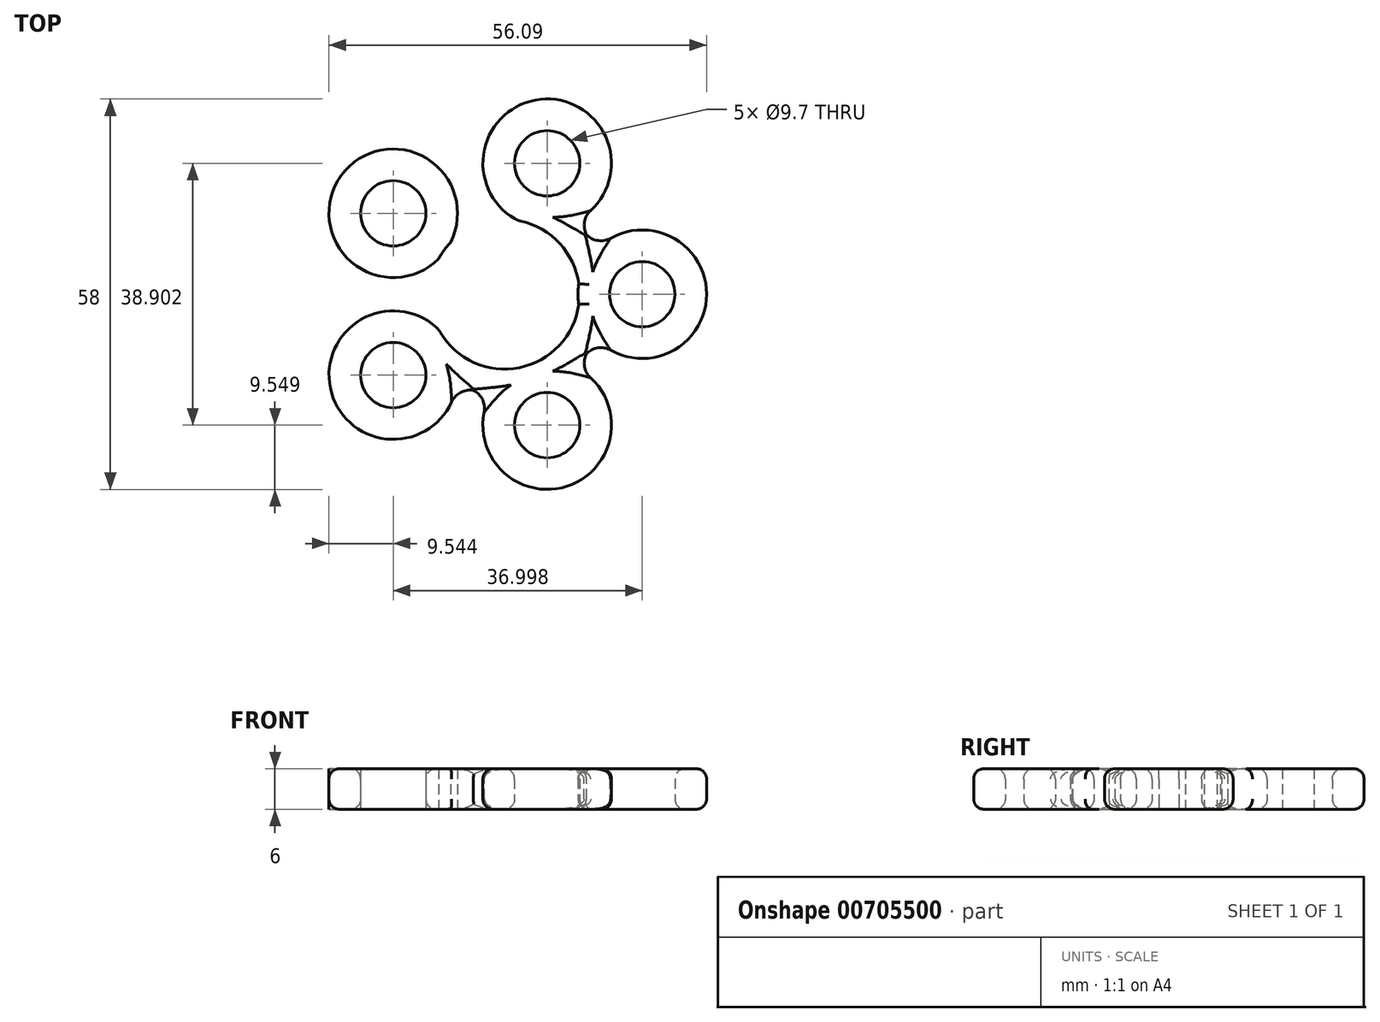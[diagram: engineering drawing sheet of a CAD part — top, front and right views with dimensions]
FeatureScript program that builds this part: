
annotation { "Feature Type Name" : "Feature", "Feature Type Description" : "" }
export const myFeature = defineFeature(function(context is Context, id is Id, definition is map)
    precondition{}
    {
        {
            var Q0;
            Q0=qCreatedBy(makeId("Top.planeOp"),FACE);
            var sketch = newSketch(context, id + "F0", { "sketchPlane" : qUnion([Q0])});
            skCircle(sketch, "E0", {"center": v(0, 0) * mm, "radius": 11.13 * mm});
            skCircle(sketch, "E1", {"center": v(0, 0) * mm, "radius": 15 * mm});
            skLineSegment(sketch, "E2", {"start": v(0, 0) * mm, "end": v(30, 0) * mm, "construction": true});
            skCircle(sketch, "E3", {"center": v(20.45, 0) * mm, "radius": 4.85 * mm});
            skCircle(sketch, "E4", {"center": v(20.45, 0) * mm, "radius": 9.55 * mm});
            skLineSegment(sketch, "E5.1.1", {"start": v(0, 0) * mm, "end": v(9.27, 28.53) * mm, "construction": true});
            skCircle(sketch, "E5.1.2", {"center": v(6.32, 19.45) * mm, "radius": 4.85 * mm});
            skCircle(sketch, "E5.1.3", {"center": v(6.32, 19.45) * mm, "radius": 9.55 * mm});
            skLineSegment(sketch, "E5.2.1", {"start": v(0, 0) * mm, "end": v(-24.27, 17.63) * mm, "construction": true});
            skCircle(sketch, "E5.2.2", {"center": v(-16.55, 12.02) * mm, "radius": 4.85 * mm});
            skCircle(sketch, "E5.2.3", {"center": v(-16.55, 12.02) * mm, "radius": 9.55 * mm});
            skLineSegment(sketch, "E6.2.3.0", {"start": v(0, 0) * mm, "end": v(-24.27, -17.63) * mm, "construction": true});
            skCircle(sketch, "E6.5.3.0", {"center": v(-16.55, -12.02) * mm, "radius": 4.85 * mm});
            skCircle(sketch, "E6.7.3.0", {"center": v(-16.55, -12.02) * mm, "radius": 9.55 * mm});
            skLineSegment(sketch, "E6.2.4.0", {"start": v(0, 0) * mm, "end": v(9.27, -28.53) * mm, "construction": true});
            skCircle(sketch, "E6.5.4.0", {"center": v(6.32, -19.45) * mm, "radius": 4.85 * mm});
            skCircle(sketch, "E6.7.4.0", {"center": v(6.32, -19.45) * mm, "radius": 9.55 * mm});
            skSolve(sketch);
        }
        {
            var Q0;
            {var subQ0=sQuery(id+"F0.wireOp",EDGE,"E1");var subQ1=sQuery(id+"F0.wireOp",EDGE,"E5.2.3");var subQ2=makeQuery(id+"F0.imprint","INTERSECT",VERTEX,{"disambiguationData":[OD(0.0)],"derivedFrom":[subQ1,subQ0]});Q0=makeQuery(id+"F0.imprint","IMPRINT",FACE,{"disambiguationData":[TD([[makeQuery(id+"F0.imprint","IMPRINT",EDGE,{"disambiguationData":[TD([[subQ2,-1.0]])],"derivedFrom":subQ1}),1.0]])]});}
            var Q1;
            {var subQ0=sQuery(id+"F0.wireOp",EDGE,"E1");var subQ1=sQuery(id+"F0.wireOp",EDGE,"E6.7.3.0");var subQ2=makeQuery(id+"F0.imprint","INTERSECT",VERTEX,{"disambiguationData":[OD(0.0)],"derivedFrom":[subQ1,subQ0]});Q1=makeQuery(id+"F0.imprint","IMPRINT",FACE,{"disambiguationData":[TD([[makeQuery(id+"F0.imprint","IMPRINT",EDGE,{"disambiguationData":[TD([[subQ2,-1.0]])],"derivedFrom":subQ1}),1.0]])]});}
            var Q2;
            {var subQ0=sQuery(id+"F0.wireOp",EDGE,"E1");var subQ1=sQuery(id+"F0.wireOp",EDGE,"E5.1.3");var subQ2=makeQuery(id+"F0.imprint","INTERSECT",VERTEX,{"disambiguationData":[OD(0.0)],"derivedFrom":[subQ1,subQ0]});Q2=makeQuery(id+"F0.imprint","IMPRINT",FACE,{"disambiguationData":[TD([[makeQuery(id+"F0.imprint","IMPRINT",EDGE,{"disambiguationData":[TD([[subQ2,-1.0]])],"derivedFrom":subQ1}),1.0]])]});}
            var Q3;
            {var subQ0=sQuery(id+"F0.wireOp",EDGE,"E1");var subQ1=sQuery(id+"F0.wireOp",EDGE,"E6.7.3.0");var subQ2=makeQuery(id+"F0.imprint","INTERSECT",VERTEX,{"disambiguationData":[OD(0.0)],"derivedFrom":[subQ1,subQ0]});Q3=makeQuery(id+"F0.imprint","IMPRINT",FACE,{"disambiguationData":[TD([[makeQuery(id+"F0.imprint","IMPRINT",EDGE,{"disambiguationData":[TD([[subQ2,-1.0]])],"derivedFrom":subQ1}),-1.0]])]});}
            var Q4;
            {var subQ0=sQuery(id+"F0.wireOp",EDGE,"E1");var subQ1=sQuery(id+"F0.wireOp",EDGE,"E4");var subQ2=makeQuery(id+"F0.imprint","INTERSECT",VERTEX,{"disambiguationData":[OD(0.0)],"derivedFrom":[subQ1,subQ0]});Q4=makeQuery(id+"F0.imprint","IMPRINT",FACE,{"disambiguationData":[TD([[makeQuery(id+"F0.imprint","IMPRINT",EDGE,{"disambiguationData":[TD([[subQ2,-1.0]])],"derivedFrom":subQ1}),1.0]])]});}
            var Q5;
            {var subQ0=sQuery(id+"F0.wireOp",EDGE,"E6.7.4.0");var subQ1=sQuery(id+"F0.wireOp",EDGE,"E1");var subQ2=makeQuery(id+"F0.imprint","INTERSECT",VERTEX,{"disambiguationData":[OD(0.0)],"derivedFrom":[subQ1,subQ0]});Q5=makeQuery(id+"F0.imprint","IMPRINT",FACE,{"disambiguationData":[TD([[makeQuery(id+"F0.imprint","IMPRINT",EDGE,{"disambiguationData":[TD([[subQ2,1.0]])],"derivedFrom":subQ1}),1.0]])]});}
            var Q6;
            Q6=makeQuery(id+"F0.imprint","IMPRINT",FACE,{"disambiguationData":[TD([[makeQuery(id+"F0.imprint","IMPRINT",EDGE,{"derivedFrom":sQuery(id+"F0.wireOp",EDGE,"E5.2.2")}),-1.0]])]});
            var Q7;
            {var subQ0=sQuery(id+"F0.wireOp",EDGE,"E1");var subQ1=sQuery(id+"F0.wireOp",EDGE,"E5.2.3");var subQ2=makeQuery(id+"F0.imprint","INTERSECT",VERTEX,{"disambiguationData":[OD(0.0)],"derivedFrom":[subQ1,subQ0]});Q7=makeQuery(id+"F0.imprint","IMPRINT",FACE,{"disambiguationData":[TD([[makeQuery(id+"F0.imprint","IMPRINT",EDGE,{"disambiguationData":[TD([[subQ2,-1.0]])],"derivedFrom":subQ1}),-1.0]])]});}
            var Q8;
            {var subQ0=sQuery(id+"F0.wireOp",EDGE,"E1");var subQ1=sQuery(id+"F0.wireOp",EDGE,"E4");var subQ2=makeQuery(id+"F0.imprint","INTERSECT",VERTEX,{"disambiguationData":[OD(0.0)],"derivedFrom":[subQ1,subQ0]});Q8=makeQuery(id+"F0.imprint","IMPRINT",FACE,{"disambiguationData":[TD([[makeQuery(id+"F0.imprint","IMPRINT",EDGE,{"disambiguationData":[TD([[subQ2,-1.0]])],"derivedFrom":subQ1}),-1.0]])]});}
            var Q9;
            Q9=makeQuery(id+"F0.imprint","IMPRINT",FACE,{"disambiguationData":[TD([[makeQuery(id+"F0.imprint","IMPRINT",EDGE,{"derivedFrom":sQuery(id+"F0.wireOp",EDGE,"E6.5.4.0")}),-1.0]])]});
            var Q10;
            Q10=makeQuery(id+"F0.imprint","IMPRINT",FACE,{"disambiguationData":[TD([[makeQuery(id+"F0.imprint","IMPRINT",EDGE,{"derivedFrom":sQuery(id+"F0.wireOp",EDGE,"E3")}),-1.0]])]});
            var Q11;
            Q11=makeQuery(id+"F0.imprint","IMPRINT",FACE,{"disambiguationData":[TD([[makeQuery(id+"F0.imprint","IMPRINT",EDGE,{"derivedFrom":sQuery(id+"F0.wireOp",EDGE,"E5.1.2")}),-1.0]])]});
            var Q12;
            {var subQ0=sQuery(id+"F0.wireOp",EDGE,"E1");var subQ1=sQuery(id+"F0.wireOp",EDGE,"E5.1.3");var subQ2=makeQuery(id+"F0.imprint","INTERSECT",VERTEX,{"disambiguationData":[OD(0.0)],"derivedFrom":[subQ1,subQ0]});Q12=makeQuery(id+"F0.imprint","IMPRINT",FACE,{"disambiguationData":[TD([[makeQuery(id+"F0.imprint","IMPRINT",EDGE,{"disambiguationData":[TD([[subQ2,-1.0]])],"derivedFrom":subQ1}),-1.0]])]});}
            var Q13;
            {var subQ0=sQuery(id+"F0.wireOp",EDGE,"E1");var subQ1=sQuery(id+"F0.wireOp",EDGE,"E4");var subQ2=makeQuery(id+"F0.imprint","INTERSECT",VERTEX,{"disambiguationData":[OD(1.0)],"derivedFrom":[subQ1,subQ0]});Q13=makeQuery(id+"F0.imprint","IMPRINT",FACE,{"disambiguationData":[TD([[makeQuery(id+"F0.imprint","IMPRINT",EDGE,{"disambiguationData":[TD([[subQ2,1.0]])],"derivedFrom":subQ1}),-1.0]])]});}
            var Q14;
            {var subQ0=sQuery(id+"F0.wireOp",EDGE,"E0");var subQ1=sQuery(id+"F0.wireOp",EDGE,"E5.1.3");var subQ2=makeQuery(id+"F0.imprint","INTERSECT",VERTEX,{"disambiguationData":[OD(0.0)],"derivedFrom":[subQ1,subQ0]});Q14=makeQuery(id+"F0.imprint","IMPRINT",FACE,{"disambiguationData":[TD([[makeQuery(id+"F0.imprint","IMPRINT",EDGE,{"disambiguationData":[TD([[subQ2,-1.0]])],"derivedFrom":subQ1}),1.0]])]});}
            var Q15;
            {var subQ0=sQuery(id+"F0.wireOp",EDGE,"E0");var subQ1=sQuery(id+"F0.wireOp",EDGE,"E6.7.4.0");var subQ2=makeQuery(id+"F0.imprint","INTERSECT",VERTEX,{"disambiguationData":[OD(0.0)],"derivedFrom":[subQ1,subQ0]});Q15=makeQuery(id+"F0.imprint","IMPRINT",FACE,{"disambiguationData":[TD([[makeQuery(id+"F0.imprint","IMPRINT",EDGE,{"disambiguationData":[TD([[subQ2,-1.0]])],"derivedFrom":subQ1}),1.0]])]});}
            var Q16;
            {var subQ0=sQuery(id+"F0.wireOp",EDGE,"E0");var subQ1=sQuery(id+"F0.wireOp",EDGE,"E4");var subQ2=makeQuery(id+"F0.imprint","INTERSECT",VERTEX,{"disambiguationData":[OD(0.0)],"derivedFrom":[subQ1,subQ0]});Q16=makeQuery(id+"F0.imprint","IMPRINT",FACE,{"disambiguationData":[TD([[makeQuery(id+"F0.imprint","IMPRINT",EDGE,{"disambiguationData":[TD([[subQ2,-1.0]])],"derivedFrom":subQ1}),1.0]])]});}
            var Q17;
            {var subQ0=sQuery(id+"F0.wireOp",EDGE,"E0");var subQ1=sQuery(id+"F0.wireOp",EDGE,"E6.7.3.0");var subQ2=makeQuery(id+"F0.imprint","INTERSECT",VERTEX,{"disambiguationData":[OD(0.0)],"derivedFrom":[subQ1,subQ0]});Q17=makeQuery(id+"F0.imprint","IMPRINT",FACE,{"disambiguationData":[TD([[makeQuery(id+"F0.imprint","IMPRINT",EDGE,{"disambiguationData":[TD([[subQ2,-1.0]])],"derivedFrom":subQ1}),1.0]])]});}
            var Q18;
            {var subQ0=sQuery(id+"F0.wireOp",EDGE,"E0");var subQ1=sQuery(id+"F0.wireOp",EDGE,"E5.2.3");var subQ2=makeQuery(id+"F0.imprint","INTERSECT",VERTEX,{"disambiguationData":[OD(0.0)],"derivedFrom":[subQ1,subQ0]});Q18=makeQuery(id+"F0.imprint","IMPRINT",FACE,{"disambiguationData":[TD([[makeQuery(id+"F0.imprint","IMPRINT",EDGE,{"disambiguationData":[TD([[subQ2,-1.0]])],"derivedFrom":subQ1}),1.0]])]});}
            var Q19;
            Q19=makeQuery(id+"F0.imprint","IMPRINT",FACE,{"disambiguationData":[TD([[makeQuery(id+"F0.imprint","IMPRINT",EDGE,{"derivedFrom":sQuery(id+"F0.wireOp",EDGE,"E6.5.3.0")}),-1.0]])]});
            extrude(context, id + "F1", {"entities" : qUnion([Q0, Q1, Q2, Q3, Q4, Q5, Q6, Q7, Q8, Q9, Q10, Q11, Q12, Q13, Q14, Q15, Q16, Q17, Q18, Q19]), "depth" : 6 * mm, "offsetDistance" : 25 * mm});
        }
        {
            var Q0;
            Q0=makeQuery(id+"F1.opExtrude","CAP_FACE",FACE,{"disambiguationData":[OSD([sQuery(id+"F0.wireOp",EDGE,"E3"),sQuery(id+"F0.wireOp",EDGE,"E4"),sQuery(id+"F0.wireOp",EDGE,"E5.1.2"),sQuery(id+"F0.wireOp",EDGE,"E5.1.3"),sQuery(id+"F0.wireOp",EDGE,"E5.2.2"),sQuery(id+"F0.wireOp",EDGE,"E5.2.3"),sQuery(id+"F0.wireOp",EDGE,"E6.5.3.0"),sQuery(id+"F0.wireOp",EDGE,"E6.7.3.0"),sQuery(id+"F0.wireOp",EDGE,"E6.5.4.0"),sQuery(id+"F0.wireOp",EDGE,"E1"),sQuery(id+"F0.wireOp",EDGE,"E6.7.4.0"),sQuery(id+"F0.wireOp",EDGE,"E0")])],"isStart":false});
            fillet(context, id + "F2", {"entities" : qUnion([Q0]), "radius" : 1.5 * mm, "tangentPropagation" : true, "allowEdgeOverflow" : false});
        }
        {
            var Q0;
            Q0=makeQuery(id+"F1.opExtrude","CAP_FACE",FACE,{"disambiguationData":[OSD([sQuery(id+"F0.wireOp",EDGE,"E3"),sQuery(id+"F0.wireOp",EDGE,"E4"),sQuery(id+"F0.wireOp",EDGE,"E5.1.2"),sQuery(id+"F0.wireOp",EDGE,"E5.1.3"),sQuery(id+"F0.wireOp",EDGE,"E5.2.2"),sQuery(id+"F0.wireOp",EDGE,"E5.2.3"),sQuery(id+"F0.wireOp",EDGE,"E6.5.3.0"),sQuery(id+"F0.wireOp",EDGE,"E6.7.3.0"),sQuery(id+"F0.wireOp",EDGE,"E6.5.4.0"),sQuery(id+"F0.wireOp",EDGE,"E1"),sQuery(id+"F0.wireOp",EDGE,"E6.7.4.0"),sQuery(id+"F0.wireOp",EDGE,"E0")])],"isStart":true});
            fillet(context, id + "F3", {"entities" : qUnion([Q0]), "radius" : 1.5 * mm, "tangentPropagation" : true, "allowEdgeOverflow" : false});
        }
        {
            var Q0;
            {var subQ0=sQuery(id+"F0.wireOp",EDGE,"E1");var subQ1=sQuery(id+"F0.wireOp",EDGE,"E6.7.3.0");Q0=makeQuery(id+"F1.opExtrude","SWEPT_FACE",FACE,{"disambiguationData":[OSD([subQ1]),TDD([makeQuery(id+"F0.imprint","IMPRINT",EDGE,{"disambiguationData":[TD([[makeQuery(id+"F0.imprint","INTERSECT",VERTEX,{"disambiguationData":[OD(0.0)],"derivedFrom":[subQ1,subQ0]}),1.0]])],"derivedFrom":subQ1})])]});}
            var Q1;
            {var subQ0=sQuery(id+"F0.wireOp",EDGE,"E1");var subQ1=sQuery(id+"F0.wireOp",EDGE,"E5.2.3");Q1=makeQuery(id+"F1.opExtrude","SWEPT_FACE",FACE,{"disambiguationData":[OSD([subQ1]),TDD([makeQuery(id+"F0.imprint","IMPRINT",EDGE,{"disambiguationData":[TD([[makeQuery(id+"F0.imprint","INTERSECT",VERTEX,{"disambiguationData":[OD(0.0)],"derivedFrom":[subQ1,subQ0]}),1.0]])],"derivedFrom":subQ1})])]});}
            var Q2;
            {var subQ0=sQuery(id+"F0.wireOp",EDGE,"E6.7.4.0");var subQ1=sQuery(id+"F0.wireOp",EDGE,"E1");Q2=makeQuery(id+"F1.opExtrude","SWEPT_FACE",FACE,{"disambiguationData":[OSD([subQ0]),TDD([makeQuery(id+"F0.imprint","IMPRINT",EDGE,{"disambiguationData":[TD([[makeQuery(id+"F0.imprint","INTERSECT",VERTEX,{"disambiguationData":[OD(0.0)],"derivedFrom":[subQ1,subQ0]}),1.0]])],"derivedFrom":subQ0})])]});}
            var Q3;
            {var subQ0=sQuery(id+"F0.wireOp",EDGE,"E1");var subQ1=sQuery(id+"F0.wireOp",EDGE,"E4");Q3=makeQuery(id+"F1.opExtrude","SWEPT_FACE",FACE,{"disambiguationData":[OSD([subQ1]),TDD([makeQuery(id+"F0.imprint","IMPRINT",EDGE,{"disambiguationData":[TD([[makeQuery(id+"F0.imprint","INTERSECT",VERTEX,{"disambiguationData":[OD(0.0)],"derivedFrom":[subQ1,subQ0]}),1.0]])],"derivedFrom":subQ1})])]});}
            var Q4;
            {var subQ0=sQuery(id+"F0.wireOp",EDGE,"E1");var subQ1=sQuery(id+"F0.wireOp",EDGE,"E5.1.3");Q4=makeQuery(id+"F1.opExtrude","SWEPT_FACE",FACE,{"disambiguationData":[OSD([subQ1]),TDD([makeQuery(id+"F0.imprint","IMPRINT",EDGE,{"disambiguationData":[TD([[makeQuery(id+"F0.imprint","INTERSECT",VERTEX,{"disambiguationData":[OD(0.0)],"derivedFrom":[subQ1,subQ0]}),1.0]])],"derivedFrom":subQ1})])]});}
            var Q5;
            {var subQ0=sQuery(id+"F0.wireOp",EDGE,"E1");Q5=makeQuery(id+"F1.opExtrude","SWEPT_FACE",FACE,{"disambiguationData":[OSD([subQ0]),TDD([makeQuery(id+"F0.imprint","IMPRINT",EDGE,{"disambiguationData":[TD([[makeQuery(id+"F0.imprint","INTERSECT",VERTEX,{"disambiguationData":[OD(0.0)],"derivedFrom":[sQuery(id+"F0.wireOp",EDGE,"E6.7.3.0"),subQ0]}),-1.0]])],"derivedFrom":subQ0})])]});}
            var Q6;
            {var subQ0=sQuery(id+"F0.wireOp",EDGE,"E1");Q6=makeQuery(id+"F1.opExtrude","SWEPT_FACE",FACE,{"disambiguationData":[OSD([subQ0]),TDD([makeQuery(id+"F0.imprint","IMPRINT",EDGE,{"disambiguationData":[TD([[makeQuery(id+"F0.imprint","INTERSECT",VERTEX,{"disambiguationData":[OD(1.0)],"derivedFrom":[sQuery(id+"F0.wireOp",EDGE,"E4"),subQ0]}),1.0]])],"derivedFrom":subQ0})])]});}
            var Q7;
            {var subQ0=sQuery(id+"F0.wireOp",EDGE,"E1");Q7=makeQuery(id+"F1.opExtrude","SWEPT_FACE",FACE,{"disambiguationData":[OSD([subQ0]),TDD([makeQuery(id+"F0.imprint","IMPRINT",EDGE,{"disambiguationData":[TD([[makeQuery(id+"F0.imprint","INTERSECT",VERTEX,{"disambiguationData":[OD(0.0)],"derivedFrom":[sQuery(id+"F0.wireOp",EDGE,"E4"),subQ0]}),-1.0]])],"derivedFrom":subQ0})])]});}
            var Q8;
            {var subQ0=sQuery(id+"F0.wireOp",EDGE,"E1");Q8=makeQuery(id+"F1.opExtrude","SWEPT_FACE",FACE,{"disambiguationData":[OSD([subQ0]),TDD([makeQuery(id+"F0.imprint","IMPRINT",EDGE,{"disambiguationData":[TD([[makeQuery(id+"F0.imprint","INTERSECT",VERTEX,{"disambiguationData":[OD(0.0)],"derivedFrom":[sQuery(id+"F0.wireOp",EDGE,"E5.1.3"),subQ0]}),-1.0]])],"derivedFrom":subQ0})])]});}
            var Q9;
            {var subQ0=sQuery(id+"F0.wireOp",EDGE,"E1");Q9=makeQuery(id+"F1.opExtrude","SWEPT_FACE",FACE,{"disambiguationData":[OSD([subQ0]),TDD([makeQuery(id+"F0.imprint","IMPRINT",EDGE,{"disambiguationData":[TD([[makeQuery(id+"F0.imprint","INTERSECT",VERTEX,{"disambiguationData":[OD(0.0)],"derivedFrom":[sQuery(id+"F0.wireOp",EDGE,"E5.2.3"),subQ0]}),-1.0]])],"derivedFrom":subQ0})])]});}
            fillet(context, id + "F4", {"entities" : qUnion([Q0, Q1, Q2, Q3, Q4, Q5, Q6, Q7, Q8, Q9]), "radius" : 3 * mm, "tangentPropagation" : true, "allowEdgeOverflow" : false});
        }
    });
